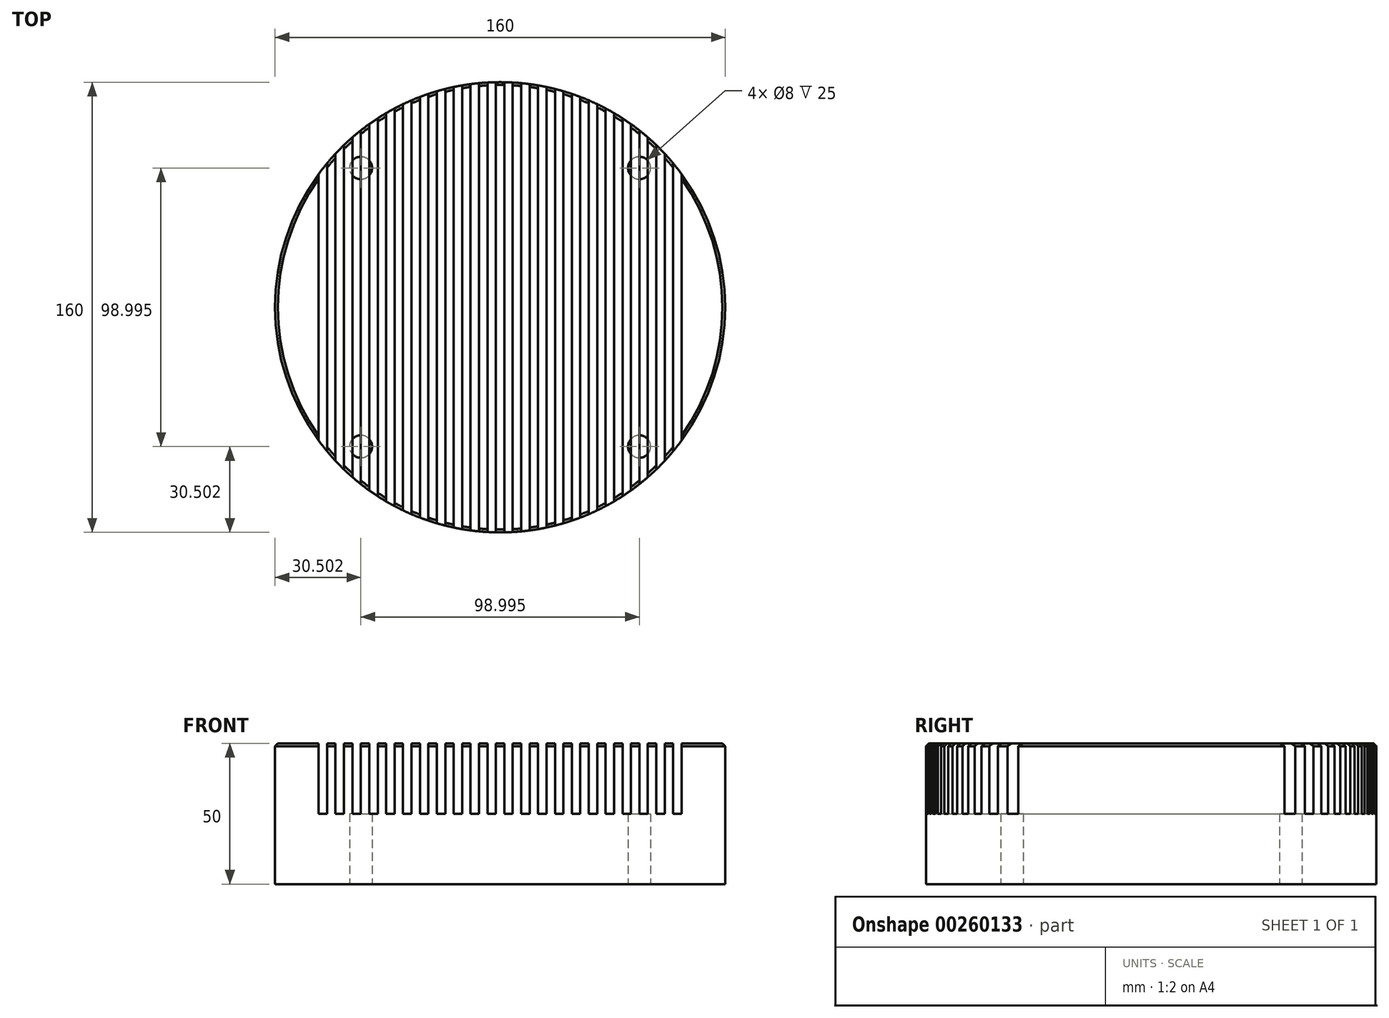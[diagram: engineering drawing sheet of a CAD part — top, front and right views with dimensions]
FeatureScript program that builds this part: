
annotation { "Feature Type Name" : "Feature", "Feature Type Description" : "" }
export const myFeature = defineFeature(function(context is Context, id is Id, definition is map)
    precondition{}
    {
        {
            var Q0;
            Q0=qCreatedBy(makeId("Top.planeOp"),FACE);
            var sketch = newSketch(context, id + "F0", { "sketchPlane" : qUnion([Q0])});
            skCircle(sketch, "E0", {"center": v(0, 0) * mm, "radius": 80 * mm});
            skSolve(sketch);
        }
        {
            var Q0;
            Q0=makeQuery(id+"F0.imprint","IMPRINT",FACE,{"disambiguationData":[TD([[makeQuery(id+"F0.imprint","IMPRINT",EDGE,{"derivedFrom":sQuery(id+"F0.wireOp",EDGE,"E0")}),1.0]])]});
            extrude(context, id + "F1", {"entities" : qUnion([Q0]), "depth" : 50 * mm});
        }
        {
            var Q0;
            Q0=qCreatedBy(makeId("Top.planeOp"),FACE);
            var sketch = newSketch(context, id + "F2", { "sketchPlane" : qUnion([Q0])});
            skCircle(sketch, "E1", {"center": v(0, 0) * mm, "radius": 70 * mm, "construction": true});
            skLineSegment(sketch, "E2", {"start": v(0, 0) * mm, "end": v(-49.5, 49.5) * mm, "construction": true});
            skCircle(sketch, "E3", {"center": v(-49.5, 49.5) * mm, "radius": 4 * mm});
            skCircle(sketch, "E4.MirrorC", {"center": v(-49.5, -49.5) * mm, "radius": 4 * mm});
            skCircle(sketch, "E5.MirrorC", {"center": v(49.5, 49.5) * mm, "radius": 4 * mm});
            skCircle(sketch, "E6.MirrorC", {"center": v(49.5, -49.5) * mm, "radius": 4 * mm});
            skSolve(sketch);
        }
        {
            var Q0;
            Q0 = qSketchRegion(id + "F2", true);
            extrude(context, id + "F3", {"entities" : qUnion([Q0]), "operationType" : NewBodyOperationType.REMOVE, "depth" : 25 * mm});
        }
        {
            var Q0;
            Q0=makeQuery(id+"F1.opExtrude","CAP_EDGE",EDGE,{"disambiguationData":[OSD([sQuery(id+"F0.wireOp",EDGE,"E0")])],"isStart":false});
            chamfer(context, id + "F4", {"entities" : qUnion([Q0]), "width" : 1 * mm, "tangentPropagation" : true});
        }
        {
            var Q0;
            Q0=qCreatedBy(makeId("Front.planeOp"),FACE);
            var sketch = newSketch(context, id + "F5", { "sketchPlane" : qUnion([Q0])});
            skLineSegment(sketch, "E7", {"start": v(0, 0) * mm, "end": v(0, 25) * mm, "construction": true});
            skLineSegment(sketch, "E8", {"start": v(-61.5, 25) * mm, "end": v(-64.5, 25) * mm});
            skLineSegment(sketch, "E9", {"start": v(-64.5, 25) * mm, "end": v(-64.5, 60) * mm});
            skLineSegment(sketch, "E10", {"start": v(-64.5, 60) * mm, "end": v(-61.5, 60) * mm});
            skLineSegment(sketch, "E11", {"start": v(-61.5, 60) * mm, "end": v(-61.5, 25) * mm});
            skLineSegment(sketch, "E12.1.0.0", {"start": v(-55.5, 60) * mm, "end": v(-55.5, 25) * mm});
            skLineSegment(sketch, "E12.1.0.1", {"start": v(-58.5, 25) * mm, "end": v(-58.5, 60) * mm});
            skLineSegment(sketch, "E12.1.0.2", {"start": v(-58.5, 60) * mm, "end": v(-55.5, 60) * mm});
            skLineSegment(sketch, "E12.1.0.3", {"start": v(-55.5, 25) * mm, "end": v(-58.5, 25) * mm});
            skLineSegment(sketch, "E12.2.0.0", {"start": v(-49.5, 60) * mm, "end": v(-49.5, 25) * mm});
            skLineSegment(sketch, "E12.2.0.1", {"start": v(-52.5, 25) * mm, "end": v(-52.5, 60) * mm});
            skLineSegment(sketch, "E12.2.0.2", {"start": v(-52.5, 60) * mm, "end": v(-49.5, 60) * mm});
            skLineSegment(sketch, "E12.2.0.3", {"start": v(-49.5, 25) * mm, "end": v(-52.5, 25) * mm});
            skLineSegment(sketch, "E12.3.0.0", {"start": v(-43.5, 60) * mm, "end": v(-43.5, 25) * mm});
            skLineSegment(sketch, "E12.3.0.1", {"start": v(-46.5, 25) * mm, "end": v(-46.5, 60) * mm});
            skLineSegment(sketch, "E12.3.0.2", {"start": v(-46.5, 60) * mm, "end": v(-43.5, 60) * mm});
            skLineSegment(sketch, "E12.3.0.3", {"start": v(-43.5, 25) * mm, "end": v(-46.5, 25) * mm});
            skLineSegment(sketch, "E12.4.0.0", {"start": v(-37.5, 60) * mm, "end": v(-37.5, 25) * mm});
            skLineSegment(sketch, "E12.4.0.1", {"start": v(-40.5, 25) * mm, "end": v(-40.5, 60) * mm});
            skLineSegment(sketch, "E12.4.0.2", {"start": v(-40.5, 60) * mm, "end": v(-37.5, 60) * mm});
            skLineSegment(sketch, "E12.4.0.3", {"start": v(-37.5, 25) * mm, "end": v(-40.5, 25) * mm});
            skLineSegment(sketch, "E12.5.0.0", {"start": v(-31.5, 60) * mm, "end": v(-31.5, 25) * mm});
            skLineSegment(sketch, "E12.5.0.1", {"start": v(-34.5, 25) * mm, "end": v(-34.5, 60) * mm});
            skLineSegment(sketch, "E12.5.0.2", {"start": v(-34.5, 60) * mm, "end": v(-31.5, 60) * mm});
            skLineSegment(sketch, "E12.5.0.3", {"start": v(-31.5, 25) * mm, "end": v(-34.5, 25) * mm});
            skLineSegment(sketch, "E12.6.0.0", {"start": v(-25.5, 60) * mm, "end": v(-25.5, 25) * mm});
            skLineSegment(sketch, "E12.6.0.1", {"start": v(-28.5, 25) * mm, "end": v(-28.5, 60) * mm});
            skLineSegment(sketch, "E12.6.0.2", {"start": v(-28.5, 60) * mm, "end": v(-25.5, 60) * mm});
            skLineSegment(sketch, "E12.6.0.3", {"start": v(-25.5, 25) * mm, "end": v(-28.5, 25) * mm});
            skLineSegment(sketch, "E12.7.0.0", {"start": v(-19.5, 60) * mm, "end": v(-19.5, 25) * mm});
            skLineSegment(sketch, "E12.7.0.1", {"start": v(-22.5, 25) * mm, "end": v(-22.5, 60) * mm});
            skLineSegment(sketch, "E12.7.0.2", {"start": v(-22.5, 60) * mm, "end": v(-19.5, 60) * mm});
            skLineSegment(sketch, "E12.7.0.3", {"start": v(-19.5, 25) * mm, "end": v(-22.5, 25) * mm});
            skLineSegment(sketch, "E12.8.0.0", {"start": v(-13.5, 60) * mm, "end": v(-13.5, 25) * mm});
            skLineSegment(sketch, "E12.8.0.1", {"start": v(-16.5, 25) * mm, "end": v(-16.5, 60) * mm});
            skLineSegment(sketch, "E12.8.0.2", {"start": v(-16.5, 60) * mm, "end": v(-13.5, 60) * mm});
            skLineSegment(sketch, "E12.8.0.3", {"start": v(-13.5, 25) * mm, "end": v(-16.5, 25) * mm});
            skLineSegment(sketch, "E12.9.0.0", {"start": v(-7.5, 60) * mm, "end": v(-7.5, 25) * mm});
            skLineSegment(sketch, "E12.9.0.1", {"start": v(-10.5, 25) * mm, "end": v(-10.5, 60) * mm});
            skLineSegment(sketch, "E12.9.0.2", {"start": v(-10.5, 60) * mm, "end": v(-7.5, 60) * mm});
            skLineSegment(sketch, "E12.9.0.3", {"start": v(-7.5, 25) * mm, "end": v(-10.5, 25) * mm});
            skLineSegment(sketch, "E12.10.0.0", {"start": v(-1.5, 60) * mm, "end": v(-1.5, 25) * mm});
            skLineSegment(sketch, "E12.10.0.1", {"start": v(-4.5, 25) * mm, "end": v(-4.5, 60) * mm});
            skLineSegment(sketch, "E12.10.0.2", {"start": v(-4.5, 60) * mm, "end": v(-1.5, 60) * mm});
            skLineSegment(sketch, "E12.10.0.3", {"start": v(-1.5, 25) * mm, "end": v(-4.5, 25) * mm});
            skLineSegment(sketch, "E12.11.0.0", {"start": v(4.5, 60) * mm, "end": v(4.5, 25) * mm});
            skLineSegment(sketch, "E12.11.0.1", {"start": v(1.5, 25) * mm, "end": v(1.5, 60) * mm});
            skLineSegment(sketch, "E12.11.0.2", {"start": v(1.5, 60) * mm, "end": v(4.5, 60) * mm});
            skLineSegment(sketch, "E12.11.0.3", {"start": v(4.5, 25) * mm, "end": v(1.5, 25) * mm});
            skLineSegment(sketch, "E12.12.0.0", {"start": v(10.5, 60) * mm, "end": v(10.5, 25) * mm});
            skLineSegment(sketch, "E12.12.0.1", {"start": v(7.5, 25) * mm, "end": v(7.5, 60) * mm});
            skLineSegment(sketch, "E12.12.0.2", {"start": v(7.5, 60) * mm, "end": v(10.5, 60) * mm});
            skLineSegment(sketch, "E12.12.0.3", {"start": v(10.5, 25) * mm, "end": v(7.5, 25) * mm});
            skLineSegment(sketch, "E12.13.0.0", {"start": v(16.5, 60) * mm, "end": v(16.5, 25) * mm});
            skLineSegment(sketch, "E12.13.0.1", {"start": v(13.5, 25) * mm, "end": v(13.5, 60) * mm});
            skLineSegment(sketch, "E12.13.0.2", {"start": v(13.5, 60) * mm, "end": v(16.5, 60) * mm});
            skLineSegment(sketch, "E12.13.0.3", {"start": v(16.5, 25) * mm, "end": v(13.5, 25) * mm});
            skLineSegment(sketch, "E12.14.0.0", {"start": v(22.5, 60) * mm, "end": v(22.5, 25) * mm});
            skLineSegment(sketch, "E12.14.0.1", {"start": v(19.5, 25) * mm, "end": v(19.5, 60) * mm});
            skLineSegment(sketch, "E12.14.0.2", {"start": v(19.5, 60) * mm, "end": v(22.5, 60) * mm});
            skLineSegment(sketch, "E12.14.0.3", {"start": v(22.5, 25) * mm, "end": v(19.5, 25) * mm});
            skLineSegment(sketch, "E12.15.0.0", {"start": v(28.5, 60) * mm, "end": v(28.5, 25) * mm});
            skLineSegment(sketch, "E12.15.0.1", {"start": v(25.5, 25) * mm, "end": v(25.5, 60) * mm});
            skLineSegment(sketch, "E12.15.0.2", {"start": v(25.5, 60) * mm, "end": v(28.5, 60) * mm});
            skLineSegment(sketch, "E12.15.0.3", {"start": v(28.5, 25) * mm, "end": v(25.5, 25) * mm});
            skLineSegment(sketch, "E12.16.0.0", {"start": v(34.5, 60) * mm, "end": v(34.5, 25) * mm});
            skLineSegment(sketch, "E12.16.0.1", {"start": v(31.5, 25) * mm, "end": v(31.5, 60) * mm});
            skLineSegment(sketch, "E12.16.0.2", {"start": v(31.5, 60) * mm, "end": v(34.5, 60) * mm});
            skLineSegment(sketch, "E12.16.0.3", {"start": v(34.5, 25) * mm, "end": v(31.5, 25) * mm});
            skLineSegment(sketch, "E12.17.0.0", {"start": v(40.5, 60) * mm, "end": v(40.5, 25) * mm});
            skLineSegment(sketch, "E12.17.0.1", {"start": v(37.5, 25) * mm, "end": v(37.5, 60) * mm});
            skLineSegment(sketch, "E12.17.0.2", {"start": v(37.5, 60) * mm, "end": v(40.5, 60) * mm});
            skLineSegment(sketch, "E12.17.0.3", {"start": v(40.5, 25) * mm, "end": v(37.5, 25) * mm});
            skLineSegment(sketch, "E12.18.0.0", {"start": v(46.5, 60) * mm, "end": v(46.5, 25) * mm});
            skLineSegment(sketch, "E12.18.0.1", {"start": v(43.5, 25) * mm, "end": v(43.5, 60) * mm});
            skLineSegment(sketch, "E12.18.0.2", {"start": v(43.5, 60) * mm, "end": v(46.5, 60) * mm});
            skLineSegment(sketch, "E12.18.0.3", {"start": v(46.5, 25) * mm, "end": v(43.5, 25) * mm});
            skLineSegment(sketch, "E12.19.0.0", {"start": v(52.5, 60) * mm, "end": v(52.5, 25) * mm});
            skLineSegment(sketch, "E12.19.0.1", {"start": v(49.5, 25) * mm, "end": v(49.5, 60) * mm});
            skLineSegment(sketch, "E12.19.0.2", {"start": v(49.5, 60) * mm, "end": v(52.5, 60) * mm});
            skLineSegment(sketch, "E12.19.0.3", {"start": v(52.5, 25) * mm, "end": v(49.5, 25) * mm});
            skLineSegment(sketch, "E12.20.0.0", {"start": v(58.5, 60) * mm, "end": v(58.5, 25) * mm});
            skLineSegment(sketch, "E12.20.0.1", {"start": v(55.5, 25) * mm, "end": v(55.5, 60) * mm});
            skLineSegment(sketch, "E12.20.0.2", {"start": v(55.5, 60) * mm, "end": v(58.5, 60) * mm});
            skLineSegment(sketch, "E12.20.0.3", {"start": v(58.5, 25) * mm, "end": v(55.5, 25) * mm});
            skLineSegment(sketch, "E12.21.0.0", {"start": v(64.5, 60) * mm, "end": v(64.5, 25) * mm});
            skLineSegment(sketch, "E12.21.0.1", {"start": v(61.5, 25) * mm, "end": v(61.5, 60) * mm});
            skLineSegment(sketch, "E12.21.0.2", {"start": v(61.5, 60) * mm, "end": v(64.5, 60) * mm});
            skLineSegment(sketch, "E12.21.0.3", {"start": v(64.5, 25) * mm, "end": v(61.5, 25) * mm});
            skLineSegment(sketch, "E12.direction1", {"start": v(-61.5, 25) * mm, "end": v(-55.5, 25) * mm, "construction": true});
            skSolve(sketch);
        }
        {
            var Q0;
            Q0 = qSketchRegion(id + "F5", true);
            extrude(context, id + "F6", {"entities" : qUnion([Q0]), "operationType" : NewBodyOperationType.REMOVE, "depth" : 100 * mm, "hasSecondDirection" : true, "secondDirectionOppositeDirection" : true, "secondDirectionDepth" : 100 * mm});
        }
    });
